# Revit family: РИДАН_Преобразователь давления MBS1700R
name_source: partatom
category: Арматура трубопроводов
units: mm (PartAtom-declared; Revit-internal decimal feet)

## family parameters
Всегда вертикально = Да
На основе рабочей плоскости = Нет
Общий = Нет
При загрузке вырезать с полостями = Нет
Размер круглого соединителя = Использовать диаметр
Тип детали = Нормальный

## types (22) — shared parameters
ADSK_Версия Revit = 2019
ADSK_Версия семейства = 1.0
ADSK_Единица измерения = шт.
ADSK_Завод-изготовитель = ООО «Ридан-Трейд»
ADSK_Количество = 1
ADSK_Марка = MBS1700R
ADSK_Масса = 0.25
LT = MBS1700R
LT1 = MBS1700R1
URL = https://ridan.ru
d = 42 мм
f = 27 мм
Изготовитель = ООО «Ридан-Трейд»

## per-type parameters (varying)
| type | ADSK_Диаметр условный | ADSK_Код изделия | ADSK_Наименование | a | b | c | e | num | num1 |
| MBS1700R 0–6 бар 4–20 мА G1/4 | 8 мм | 060G6100R | Преобразователь (датчик) давления MBS1700R 0–6 бар, 4–20 мА, G1/4 | 79 мм | 65 мм | 56 мм | 13 мм | 2 | 1 |
| MBS1700R 0–10 бар 4–20 мА G1/4 | 8 мм | 060G6101R | Преобразователь (датчик) давления MBS1700R 0–10 бар, 4–20 мА, G1/4 | 79 мм | 65 мм | 56 мм | 13 мм | 2 | 2 |
| MBS1700R 0–16 бар 4–20 мА G1/4 | 8 мм | 060G6102R | Преобразователь (датчик) давления MBS1700R 0–16 бар, 4–20 мА, G1/4 | 79 мм | 65 мм | 56 мм | 13 мм | 2 | 3 |
| MBS1700R 0–25 бар 4–20 мА G1/4 | 8 мм | 060G6103R | Преобразователь (датчик) давления MBS1700R 0–25 бар, 4–20 мА, G1/4 | 79 мм | 65 мм | 56 мм | 13 мм | 2 | 4 |
| MBS1700R 0–40 бар 4–20 мА G1/4 | 8 мм | 060G6113R | Преобразователь (датчик) давления MBS1700R 0–40 бар, 4–20 мА, G1/4 | 79 мм | 65 мм | 56 мм | 13 мм | 2 | 5 |
| MBS1700R 0–6 бар 4–20 мА G1/2 | 15 мм | 060G6104R | Преобразователь (датчик) давления MBS1700R 0–6 бар, 4–20 мА, G1/2 | 86 мм | 68 мм | 59 мм | 20 мм | 3 | 6 |
| MBS1700R 0–10 бар 4–20 мА G1/2 | 15 мм | 060G6105R | Преобразователь (датчик) давления MBS1700R 0–10 бар, 4–20 мА, G1/2 | 86 мм | 68 мм | 59 мм | 20 мм | 3 | 7 |
| MBS1700R 0–16 бар 4–20 мА G1/2 | 15 мм | 060G6106R | Преобразователь (датчик) давления MBS1700R 0–16 бар, 4–20 мА, G1/2 | 86 мм | 68 мм | 59 мм | 20 мм | 3 | 8 |
| MBS1700R 0–25 бар 4–20 мА G1/2 | 15 мм | 060G6107R | Преобразователь (датчик) давления MBS1700R 0–25 бар, 4–20 мА, G1/2 | 86 мм | 68 мм | 59 мм | 20 мм | 3 | 9 |
| MBS1700R 0–40 бар 4–20 мА G1/2 | 15 мм | 060G6114R | Преобразователь (датчик) давления MBS1700R 0–40 бар, 4–20 мА, G1/2 | 86 мм | 68 мм | 59 мм | 20 мм | 3 | 10 |
| MBS1700R 0–60 бар 4–20 мА G1/4 | 8 мм | 060G6108R | Преобразователь (датчик) давления MBS1700R 0–60 бар, 4–20 мА, G1/4 | 79 мм | 65 мм | 56 мм | 13 мм | 2 | 11 |
| MBS1700R 0-100 бар 4–20 мА G1/4 | 8 мм | 060G6112R | Преобразователь (датчик) давления MBS1700R 0-100 бар, 4–20 мА, G1/4 | 79 мм | 65 мм | 56 мм | 13 мм | 2 | 12 |
| MBS1700R 0-160 бар 4–20 мА G1/4 | 8 мм | 060G6109R | Преобразователь (датчик) давления MBS1700R 0-160 бар, 4–20 мА, G1/4 | 79 мм | 65 мм | 56 мм | 13 мм | 2 | 13 |
| MBS1700R 0-250 бар 4–20 мА G1/4 | 8 мм | 060G6110R | Преобразователь (датчик) давления MBS1700R 0-250 бар, 4–20 мА, G1/4 | 79 мм | 65 мм | 56 мм | 13 мм | 2 | 14 |
| MBS1700R 0-400 бар 4–20 мА G1/4 | 8 мм | 060G6111R | Преобразователь (датчик) давления MBS1700R 0-400 бар, 4–20 мА, G1/4 | 79 мм | 65 мм | 56 мм | 13 мм | 2 | 15 |
| MBS1700R 0–6 бар 4–20 мА М20×1,5 | 15 мм | 060G3820R | Преобразователь (датчик) давления MBS1700R 0–6 бар, 4–20 мА, М20*1 5 | 86 мм | 68 мм | 59 мм | 20 мм | 1 | 16 |
| MBS1700R 0-10 бар 4–20 мА М20×1,5 | 15 мм | 060G3821R | Преобразователь (датчик) давления MBS1700R 0-10 бар, 4–20 мА, М20*1 5 | 86 мм | 68 мм | 59 мм | 20 мм | 1 | 17 |
| MBS1700R 0-16 бар 4–20 мА М20×1,5 | 15 мм | 060G3822R | Преобразователь (датчик) давления MBS1700R 0-16 бар, 4–20 мА, М20*1 5 | 86 мм | 68 мм | 59 мм | 20 мм | 1 | 18 |
| MBS1700R 0–6 бар 0–10 В G1/2 | 15 мм | 060G6204R | Преобразователь (датчик) давления MBS1700R 0–6 бар, 0-10 В, G1/4 | 86 мм | 68 мм | 59 мм | 20 мм | 3 | 19 |
| MBS1700R 0–10 бар 0–10 В G1/2 | 15 мм | 060G6205R | Преобразователь (датчик) давления MBS1700R 0–10 бар, 0-10 В, G1/4 | 86 мм | 68 мм | 59 мм | 20 мм | 3 | 20 |
| MBS1700R 0–16 бар 0–10 В G1/2 | 15 мм | 060G6206R | Преобразователь (датчик) давления MBS1700R 0–16 бар, 0-10 В, G1/4 | 86 мм | 68 мм | 59 мм | 20 мм | 3 | 21 |
| MBS1700R 0–25 бар 0–10 В G1/2 | 15 мм | 060G6207R | Преобразователь (датчик) давления MBS1700R 0–25 бар, 0-10 В, G1/4 | 86 мм | 68 мм | 59 мм | 20 мм | 3 | 22 |
